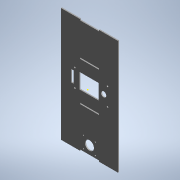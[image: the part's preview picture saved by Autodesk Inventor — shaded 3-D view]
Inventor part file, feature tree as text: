
AUTODESK INVENTOR PART (.ipt)
format: ipt  version: 2020 (Build 240168000, 168)  size: 209,408 bytes
history: native  units: mm (DEFAULTED — no unit token found)
features: sketch x20, extrude x16
ambient origin geometry x8: Origin, YZ Plane, XZ Plane, XY Plane, X Axis, Y Axis, Z Axis, Center Point
bodies: Solid1 (feature_tree)
feature tree (36):
  extrude  "Extrusion1"  Depth=50.0mm
  sketch  "3D Sketch1"
  extrude  "Extrusion2"  Depth=3.0mm TaperAngle=0.0deg
  extrude  "Extrusion3"  Depth=3.0mm TaperAngle=0.0deg
  extrude  "Extrusion4"  Depth=3.0mm TaperAngle=0.0deg
  extrude  "Extrusion5"  Depth=3.0mm TaperAngle=0.0deg
  extrude  "Extrusion6"  Depth=10.0mm
  extrude  "Extrusion7"  Depth=31.999867mm
  extrude  "Extrusion8"  Depth=3.0mm TaperAngle=0.0deg
  sketch  "Sketch9"  dims[d114=3.0mm d115=0.0mm d116=3.0mm d117=0.0mm]
  sketch  "Sketch10"  dims[d118=3.0mm d119=0.0mm d133=35.75mm d134=0.0mm]
  extrude  "Extrusion9"  Depth=3.0mm TaperAngle=0.0deg
  extrude  "Extrusion10"  Depth=35.75mm TaperAngle=0.0deg
  extrude  "Extrusion11"  [1 undecoded]
  extrude  "Extrusion12"  [1 undecoded]
  extrude  "Extrusion13"  [1 undecoded]
  extrude  "Extrusion14"  [1 undecoded]
  extrude  "Extrusion15"  [1 undecoded]
  extrude  "Extrusion16"  [1 undecoded]
  sketch  "Sketch19"
  sketch  "Sketch1"  dims[d2=3.0mm d3=0.0mm d9=50.0mm]
  sketch  "Sketch2"  dims[d14=3.0mm d15=0.0mm d21=3.0mm d22=0.0mm]
  sketch  "Sketch3"  dims[d25=3.0mm d26=0.0mm d31=3.0mm d32=0.0mm]
  sketch  "Sketch4"  dims[d37=3.0mm d38=0.0mm d45=3.0mm d46=0.0mm]
  sketch  "Sketch5"  dims[d58=3.0mm d59=0.0mm d102=30.0mm d103=0.0mm]
  sketch  "Sketch6"  dims[d104=10.0mm d105=0.0mm d107=15.0mm]
  sketch  "Sketch7"  dims[d108=32.056514mm d109=31.999867mm]
  sketch  "Sketch8"  dims[d110=3.0mm d111=0.0mm d112=3.0mm d113=0.0mm]
  sketch  "Sketch11"
  sketch  "Sketch12"
  sketch  "Sketch13"
  sketch  "Sketch14"
  sketch  "Sketch15"
  sketch  "Sketch16"
  sketch  "Sketch17"
  sketch  "Sketch18"
note: 6 required parameter values undecoded (feature->parameter linkage not recoverable at this tier; creation-order binding heuristic only, values carry confidence <= 0.55)
